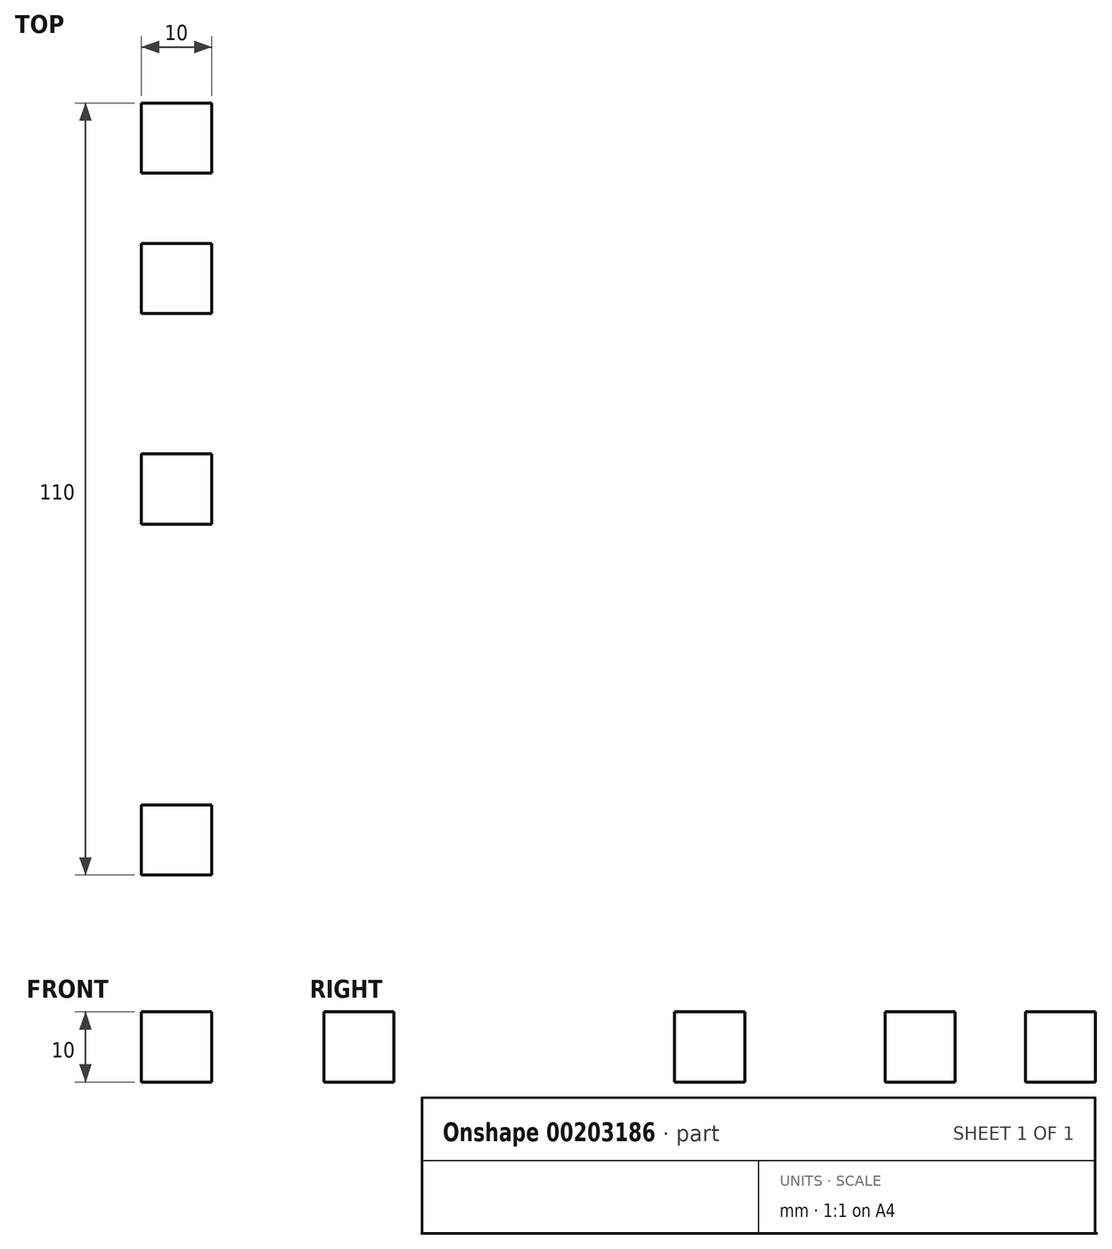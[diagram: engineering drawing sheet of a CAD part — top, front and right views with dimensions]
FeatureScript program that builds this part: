
annotation { "Feature Type Name" : "Feature", "Feature Type Description" : "" }
export const myFeature = defineFeature(function(context is Context, id is Id, definition is map)
    precondition{}
    {
        {
            var Q0;
            Q0=qCreatedBy(makeId("Right.planeOp"),FACE);
            var sketch = newSketch(context, id + "F0", { "sketchPlane" : qUnion([Q0])});
            skLineSegment(sketch, "E0.bottom", {"start": v(45.26, 0) * mm, "end": v(35.26, 0) * mm});
            skLineSegment(sketch, "E0.top", {"start": v(45.26, 10) * mm, "end": v(35.26, 10) * mm});
            skLineSegment(sketch, "E0.left", {"start": v(45.26, 0) * mm, "end": v(45.26, 10) * mm});
            skLineSegment(sketch, "E0.right", {"start": v(35.26, 0) * mm, "end": v(35.26, 10) * mm});
            skLineSegment(sketch, "E1.bottom", {"start": v(25.26, 0) * mm, "end": v(15.26, 0) * mm});
            skLineSegment(sketch, "E1.top", {"start": v(25.26, 10) * mm, "end": v(15.26, 10) * mm});
            skLineSegment(sketch, "E1.left", {"start": v(25.26, 0) * mm, "end": v(25.26, 10) * mm});
            skLineSegment(sketch, "E1.right", {"start": v(15.26, 0) * mm, "end": v(15.26, 10) * mm});
            skLineSegment(sketch, "E2.bottom", {"start": v(-4.74, 0) * mm, "end": v(-14.74, 0) * mm});
            skLineSegment(sketch, "E2.top", {"start": v(-4.74, 10) * mm, "end": v(-14.74, 10) * mm});
            skLineSegment(sketch, "E2.left", {"start": v(-4.74, 0) * mm, "end": v(-4.74, 10) * mm});
            skLineSegment(sketch, "E2.right", {"start": v(-14.74, 0) * mm, "end": v(-14.74, 10) * mm});
            skLineSegment(sketch, "E3.bottom", {"start": v(-54.74, 0) * mm, "end": v(-64.74, 0) * mm});
            skLineSegment(sketch, "E3.top", {"start": v(-54.74, 10) * mm, "end": v(-64.74, 10) * mm});
            skLineSegment(sketch, "E3.left", {"start": v(-54.74, 0) * mm, "end": v(-54.74, 10) * mm});
            skLineSegment(sketch, "E3.right", {"start": v(-64.74, 0) * mm, "end": v(-64.74, 10) * mm});
            skSolve(sketch);
        }
        {
            var Q0;
            Q0=makeQuery(id+"F0.imprint","IMPRINT",FACE,{"disambiguationData":[TD([[makeQuery(id+"F0.imprint","IMPRINT",EDGE,{"derivedFrom":sQuery(id+"F0.wireOp",EDGE,"E3.bottom")}),-1.0]])]});
            var Q1;
            Q1=makeQuery(id+"F0.imprint","IMPRINT",FACE,{"disambiguationData":[TD([[makeQuery(id+"F0.imprint","IMPRINT",EDGE,{"derivedFrom":sQuery(id+"F0.wireOp",EDGE,"E2.bottom")}),-1.0]])]});
            var Q2;
            Q2=makeQuery(id+"F0.imprint","IMPRINT",FACE,{"disambiguationData":[TD([[makeQuery(id+"F0.imprint","IMPRINT",EDGE,{"derivedFrom":sQuery(id+"F0.wireOp",EDGE,"E1.bottom")}),-1.0]])]});
            var Q3;
            Q3=makeQuery(id+"F0.imprint","IMPRINT",FACE,{"disambiguationData":[TD([[makeQuery(id+"F0.imprint","IMPRINT",EDGE,{"derivedFrom":sQuery(id+"F0.wireOp",EDGE,"E0.bottom")}),-1.0]])]});
            extrude(context, id + "F1", {"entities" : qUnion([Q0, Q1, Q2, Q3]), "depth" : 10 * mm});
        }
    });
